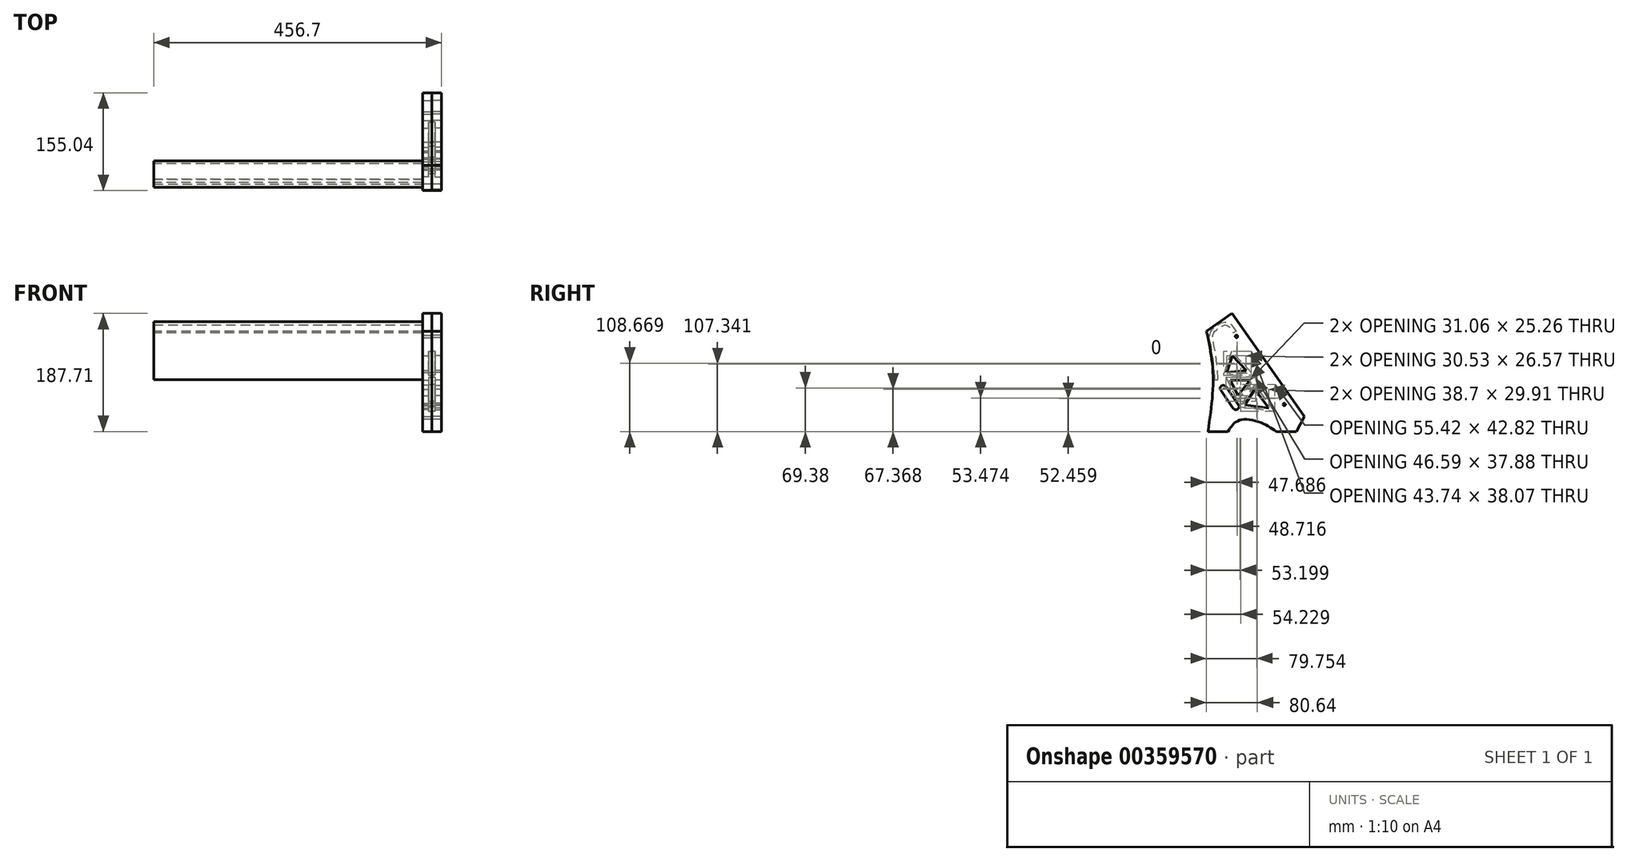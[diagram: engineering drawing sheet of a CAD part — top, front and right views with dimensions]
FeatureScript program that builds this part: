
annotation { "Feature Type Name" : "Feature", "Feature Type Description" : "" }
export const myFeature = defineFeature(function(context is Context, id is Id, definition is map)
    precondition{}
    {
        {
            var Q0;
            Q0=qCreatedBy(makeId("Right.planeOp"),FACE);
            var sketch = newSketch(context, id + "F0", { "sketchPlane" : qUnion([Q0])});
            skLineSegment(sketch, "E0", {"start": v(78.73, -61.03) * mm, "end": v(66.43, -84.9) * mm});
            skLineSegment(sketch, "E1", {"start": v(66.43, -84.9) * mm, "end": v(34.56, -84.9) * mm});
            skLineSegment(sketch, "E2", {"start": v(-35.98, 102.8) * mm, "end": v(-76.31, 74.53) * mm});
            skLineSegment(sketch, "E3", {"start": v(-35.98, 102.8) * mm, "end": v(78.73, -61.03) * mm});
            skLineSegment(sketch, "E4", {"start": v(-74.1, -84.9) * mm, "end": v(-42.24, -84.9) * mm});
            skFitSpline(sketch, "E5", {"points": [v(-42.24, -84.9) * mm, v(-32.6, -71.97) * mm, v(-16.64, -65.56) * mm, v(13.5, -72.27) * mm, v(34.56, -84.9) * mm], "startDerivative": vector(37.12, 66.33) * mm, "endDerivative": vector(75.27, -49.53) * mm});
            skFitSpline(sketch, "E6", {"points": [v(-76.31, 74.53) * mm, v(-65.92, 4.07) * mm, v(-74.1, -84.9) * mm], "startDerivative": vector(30.89, -144.9) * mm, "endDerivative": vector(-25.41, -173.45) * mm});
            skPoint(sketch, "E7", {"position": v(47, -41.88) * mm});
            skCircle(sketch, "E8", {"center": v(47, -41.88) * mm, "radius": 2 * mm});
            skLineSegment(sketch, "E9", {"start": v(47, -41.88) * mm, "end": v(-28.74, 66.23) * mm, "construction": true});
            skCircle(sketch, "E10", {"center": v(-28.74, 66.23) * mm, "radius": 2 * mm});
            skLineSegment(sketch, "E11", {"start": v(47, -41.88) * mm, "end": v(59.29, -33.27) * mm, "construction": true});
            skSolve(sketch);
        }
        {
            var Q0;
            Q0 = qSketchRegion(id + "F0", true);
            extrude(context, id + "F1", {"entities" : qUnion([Q0]), "oppositeDirection" : true, "depth" : 15 * mm});
        }
        {
            var Q0;
            Q0=makeQuery(id+"F1.opExtrude","CAP_FACE",FACE,{"disambiguationData":[OSD([sQuery(id+"F0.wireOp",EDGE,"E0"),sQuery(id+"F0.wireOp",EDGE,"E1"),sQuery(id+"F0.wireOp",EDGE,"E2"),sQuery(id+"F0.wireOp",EDGE,"E3"),sQuery(id+"F0.wireOp",EDGE,"E4"),sQuery(id+"F0.wireOp",EDGE,"E5"),sQuery(id+"F0.wireOp",EDGE,"E6")])],"isStart":false});
            var sketch = newSketch(context, id + "F2", { "sketchPlane" : qUnion([Q0])});
            skLineSegment(sketch, "E12.bottom", {"start": v(48.52, -9.48) * mm, "end": v(56.7, -15.21) * mm});
            skLineSegment(sketch, "E12.top", {"start": v(22.7, -46.34) * mm, "end": v(30.9, -52.08) * mm});
            skLineSegment(sketch, "E12.left", {"start": v(48.52, -9.48) * mm, "end": v(22.7, -46.34) * mm});
            skLineSegment(sketch, "E12.right", {"start": v(56.7, -15.21) * mm, "end": v(30.9, -52.08) * mm});
            skSolve(sketch);
        }
        {
            var Q0;
            Q0=makeQuery(id+"F2.imprint","IMPRINT",FACE,{"disambiguationData":[TD([[makeQuery(id+"F2.imprint","IMPRINT",EDGE,{"derivedFrom":sQuery(id+"F2.wireOp",EDGE,"E12.bottom")}),-1.0]])]});
            extrude(context, id + "F3", {"entities" : qUnion([Q0]), "operationType" : NewBodyOperationType.REMOVE, "oppositeDirection" : true, "depth" : 10 * mm});
        }
        {
            var Q0;
            Q0=makeQuery(id+"F3.boolean.opBoolean","COPY",EDGE,{"derivedFrom":makeQuery(id+"F3.opExtrude","SWEPT_EDGE",EDGE,{"disambiguationData":[OSD([sQuery(id+"F2.wireOp",EDGE,"E12.bottom"),sQuery(id+"F2.wireOp",EDGE,"E12.left")])]})});
            var Q1;
            Q1=makeQuery(id+"F3.boolean.opBoolean","COPY",EDGE,{"derivedFrom":makeQuery(id+"F3.opExtrude","SWEPT_EDGE",EDGE,{"disambiguationData":[OSD([sQuery(id+"F2.wireOp",EDGE,"E12.bottom"),sQuery(id+"F2.wireOp",EDGE,"E12.right")])]})});
            var Q2;
            Q2=makeQuery(id+"F3.boolean.opBoolean","COPY",EDGE,{"derivedFrom":makeQuery(id+"F3.opExtrude","SWEPT_EDGE",EDGE,{"disambiguationData":[OSD([sQuery(id+"F2.wireOp",EDGE,"E12.top"),sQuery(id+"F2.wireOp",EDGE,"E12.right")])]})});
            var Q3;
            Q3=makeQuery(id+"F3.boolean.opBoolean","COPY",EDGE,{"derivedFrom":makeQuery(id+"F3.opExtrude","SWEPT_EDGE",EDGE,{"disambiguationData":[OSD([sQuery(id+"F2.wireOp",EDGE,"E12.top"),sQuery(id+"F2.wireOp",EDGE,"E12.left")])]})});
            fillet(context, id + "F4", {"entities" : qUnion([Q0, Q1, Q2, Q3]), "radius" : 5 * mm, "tangentPropagation" : true, "allowEdgeOverflow" : false});
        }
        {
            var Q0;
            Q0=makeQuery(id+"F1.opExtrude","CAP_FACE",FACE,{"disambiguationData":[OSD([sQuery(id+"F0.wireOp",EDGE,"E0"),sQuery(id+"F0.wireOp",EDGE,"E1"),sQuery(id+"F0.wireOp",EDGE,"E2"),sQuery(id+"F0.wireOp",EDGE,"E3"),sQuery(id+"F0.wireOp",EDGE,"E4"),sQuery(id+"F0.wireOp",EDGE,"E5"),sQuery(id+"F0.wireOp",EDGE,"E6")])],"isStart":true});
            var sketch = newSketch(context, id + "F5", { "sketchPlane" : qUnion([Q0])});
            skLineSegment(sketch, "E13", {"start": v(-36.7, 42.8) * mm, "end": v(-49.46, 4.73) * mm});
            skLineSegment(sketch, "E14", {"start": v(-49.46, 4.73) * mm, "end": v(-5.72, 8.98) * mm});
            skLineSegment(sketch, "E15", {"start": v(-5.72, 8.98) * mm, "end": v(-36.7, 42.8) * mm});
            skLineSegment(sketch, "E16", {"start": v(-34.98, 35.71) * mm, "end": v(-43.89, 9.15) * mm});
            skLineSegment(sketch, "E17", {"start": v(-43.89, 9.15) * mm, "end": v(-13.36, 12.12) * mm});
            skLineSegment(sketch, "E18", {"start": v(-13.36, 12.12) * mm, "end": v(-34.98, 35.71) * mm});
            skLineSegment(sketch, "E19", {"start": v(-45.38, 1.4) * mm, "end": v(-27.44, -36.48) * mm});
            skLineSegment(sketch, "E20", {"start": v(-27.44, -36.48) * mm, "end": v(1.22, 1.4) * mm});
            skLineSegment(sketch, "E21", {"start": v(1.22, 1.4) * mm, "end": v(-45.38, 1.4) * mm});
            skLineSegment(sketch, "E22", {"start": v(-38.64, -2.9) * mm, "end": v(-7.58, -2.9) * mm});
            skLineSegment(sketch, "E23", {"start": v(-7.58, -2.9) * mm, "end": v(-26.69, -28.16) * mm});
            skLineSegment(sketch, "E24", {"start": v(-26.69, -28.16) * mm, "end": v(-38.64, -2.9) * mm});
            skLineSegment(sketch, "E25", {"start": v(0.13, -10.02) * mm, "end": v(-23.38, -45.4) * mm});
            skLineSegment(sketch, "E26", {"start": v(-23.38, -45.4) * mm, "end": v(32.04, -52.85) * mm});
            skLineSegment(sketch, "E27", {"start": v(32.04, -52.85) * mm, "end": v(0.13, -10.02) * mm});
            skLineSegment(sketch, "E28", {"start": v(-15.9, -42.2) * mm, "end": v(0.51, -17.5) * mm});
            skLineSegment(sketch, "E29", {"start": v(0.51, -17.5) * mm, "end": v(22.8, -47.4) * mm});
            skLineSegment(sketch, "E30", {"start": v(22.8, -47.4) * mm, "end": v(-15.9, -42.2) * mm});
            skSolve(sketch);
        }
        {
            var Q0;
            Q0=makeQuery(id+"F5.imprint","IMPRINT",FACE,{"disambiguationData":[TD([[makeQuery(id+"F5.imprint","IMPRINT",EDGE,{"derivedFrom":sQuery(id+"F5.wireOp",EDGE,"E16")}),1.0]])]});
            extrude(context, id + "F6", {"entities" : qUnion([Q0]), "operationType" : NewBodyOperationType.REMOVE, "endBound" : BoundingType.UP_TO_NEXT, "oppositeDirection" : true, "depth" : 25 * mm});
        }
        {
            var Q0;
            Q0=makeQuery(id+"F5.imprint","IMPRINT",FACE,{"disambiguationData":[TD([[makeQuery(id+"F5.imprint","IMPRINT",EDGE,{"derivedFrom":sQuery(id+"F5.wireOp",EDGE,"E13")}),1.0]])]});
            extrude(context, id + "F7", {"entities" : qUnion([Q0]), "operationType" : NewBodyOperationType.REMOVE, "oppositeDirection" : true, "depth" : 5 * mm});
        }
        {
            var Q0;
            Q0=makeQuery(id+"F5.imprint","IMPRINT",FACE,{"disambiguationData":[TD([[makeQuery(id+"F5.imprint","IMPRINT",EDGE,{"derivedFrom":sQuery(id+"F5.wireOp",EDGE,"E22")}),-1.0]])]});
            extrude(context, id + "F8", {"entities" : qUnion([Q0]), "operationType" : NewBodyOperationType.REMOVE, "endBound" : BoundingType.UP_TO_NEXT, "oppositeDirection" : true, "depth" : 25 * mm});
        }
        {
            var Q0;
            Q0=makeQuery(id+"F5.imprint","IMPRINT",FACE,{"disambiguationData":[TD([[makeQuery(id+"F5.imprint","IMPRINT",EDGE,{"derivedFrom":sQuery(id+"F5.wireOp",EDGE,"E19")}),1.0]])]});
            extrude(context, id + "F9", {"entities" : qUnion([Q0]), "operationType" : NewBodyOperationType.REMOVE, "oppositeDirection" : true, "depth" : 5 * mm});
        }
        {
            var Q0;
            Q0=makeQuery(id+"F5.imprint","IMPRINT",FACE,{"disambiguationData":[TD([[makeQuery(id+"F5.imprint","IMPRINT",EDGE,{"derivedFrom":sQuery(id+"F5.wireOp",EDGE,"E28")}),-1.0]])]});
            extrude(context, id + "F10", {"entities" : qUnion([Q0]), "operationType" : NewBodyOperationType.REMOVE, "endBound" : BoundingType.UP_TO_NEXT, "oppositeDirection" : true, "depth" : 25 * mm});
        }
        {
            var Q0;
            Q0=makeQuery(id+"F5.imprint","IMPRINT",FACE,{"disambiguationData":[TD([[makeQuery(id+"F5.imprint","IMPRINT",EDGE,{"derivedFrom":sQuery(id+"F5.wireOp",EDGE,"E25")}),1.0]])]});
            extrude(context, id + "F11", {"entities" : qUnion([Q0]), "operationType" : NewBodyOperationType.REMOVE, "oppositeDirection" : true, "depth" : 5 * mm});
        }
        {
            var Q0;
            Q0=makeQuery(id+"F1.opExtrude","CAP_FACE",FACE,{"disambiguationData":[OSD([sQuery(id+"F0.wireOp",EDGE,"E0"),sQuery(id+"F0.wireOp",EDGE,"E1"),sQuery(id+"F0.wireOp",EDGE,"E2"),sQuery(id+"F0.wireOp",EDGE,"E3"),sQuery(id+"F0.wireOp",EDGE,"E4"),sQuery(id+"F0.wireOp",EDGE,"E5"),sQuery(id+"F0.wireOp",EDGE,"E6"),sQuery(id+"F0.wireOp",EDGE,"E8"),sQuery(id+"F0.wireOp",EDGE,"E10")])],"isStart":false});
            var sketch = newSketch(context, id + "F12", { "sketchPlane" : qUnion([Q0])});
            skFitSpline(sketch, "E31", {"points": [v(60.6, -2.7) * mm, v(61.95, 20.43) * mm, v(65.38, 43.8) * mm, v(67.74, 57.6) * mm, v(68.1, 70.07) * mm, v(60.85, 79.49) * mm, v(45.29, 86.54) * mm, v(31.78, 72.65) * mm], "startDerivative": vector(-3.94, 91.78) * mm, "endDerivative": vector(-94.96, -155.93) * mm});
            skSolve(sketch);
        }
        {
            var Q0;
            Q0=qCreatedBy(makeId("Top.planeOp"),FACE);
            var sketch = newSketch(context, id + "F13", { "sketchPlane" : qUnion([Q0])});
            skLineSegment(sketch, "E32.bottom", {"start": v(-15, -63.27) * mm, "end": v(-441.7, -63.27) * mm});
            skLineSegment(sketch, "E32.top", {"start": v(-15, -58.27) * mm, "end": v(-441.7, -58.27) * mm});
            skLineSegment(sketch, "E32.left", {"start": v(-15, -63.27) * mm, "end": v(-15, -58.27) * mm});
            skLineSegment(sketch, "E32.right", {"start": v(-441.7, -63.27) * mm, "end": v(-441.7, -58.27) * mm});
            skSolve(sketch);
        }
        {
            var Q0;
            Q0=makeQuery(id+"F13.imprint","IMPRINT",FACE,{"disambiguationData":[TD([[makeQuery(id+"F13.imprint","IMPRINT",EDGE,{"derivedFrom":sQuery(id+"F13.wireOp",EDGE,"E32.bottom")}),-1.0]])]});
            var Q1;
            Q1=sQuery(id+"F12.wireOp",EDGE,"E31");
            sweep(context, id + "F14", {"profiles" : qUnion([Q0]), "path" : qUnion([Q1])});
        }
        {
            var Q0;
            Q0=makeQuery(id+"F1.opExtrude","SWEPT_BODY",BODY,{"disambiguationData":[OSD([sQuery(id+"F0.wireOp",EDGE,"E0"),sQuery(id+"F0.wireOp",EDGE,"E1"),sQuery(id+"F0.wireOp",EDGE,"E2"),sQuery(id+"F0.wireOp",EDGE,"E3"),sQuery(id+"F0.wireOp",EDGE,"E4"),sQuery(id+"F0.wireOp",EDGE,"E5"),sQuery(id+"F0.wireOp",EDGE,"E6"),sQuery(id+"F0.wireOp",EDGE,"E8"),sQuery(id+"F0.wireOp",EDGE,"E10")])]});
            var Q1;
            Q1=qCreatedBy(makeId("Right.planeOp"),FACE);
            mirror(context, id + "F15", {"entities" : qUnion([Q0]), "mirrorPlane" : qUnion([Q1])});
        }
    });
